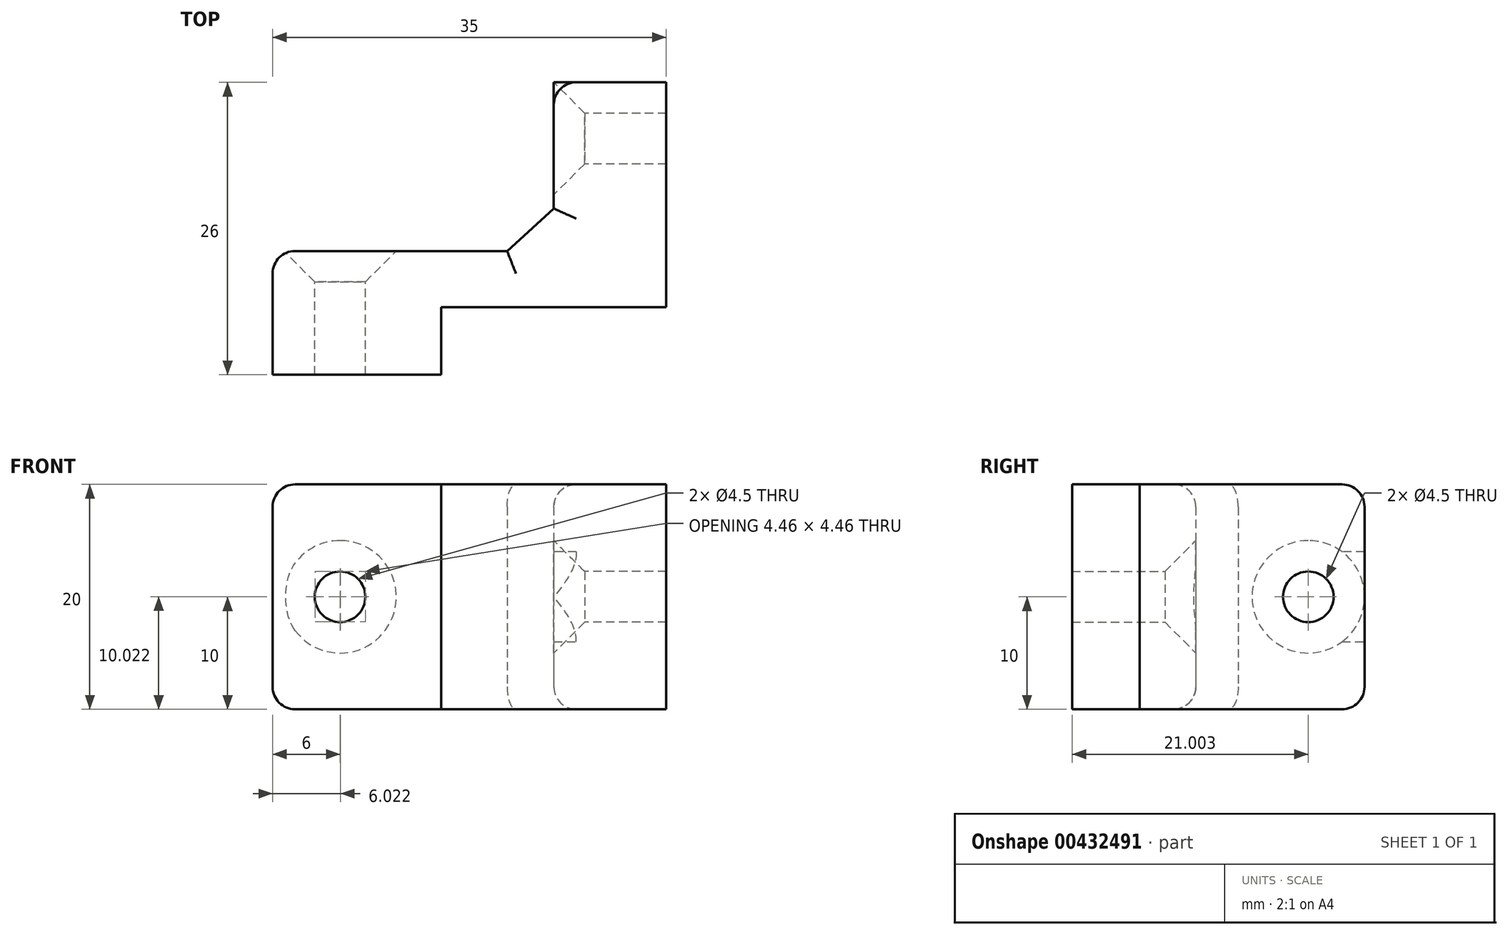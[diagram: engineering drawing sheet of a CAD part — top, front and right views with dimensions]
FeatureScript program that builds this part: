
annotation { "Feature Type Name" : "Feature", "Feature Type Description" : "" }
export const myFeature = defineFeature(function(context is Context, id is Id, definition is map)
    precondition{}
    {
        {
            var Q0;
            Q0=qCreatedBy(makeId("Top.planeOp"),FACE);
            var sketch = newSketch(context, id + "F0", { "sketchPlane" : qUnion([Q0])});
            skLineSegment(sketch, "E0", {"start": v(10, 0.5) * mm, "end": v(10, 20.5) * mm});
            skLineSegment(sketch, "E1", {"start": v(10, 20.5) * mm, "end": v(0, 20.5) * mm});
            skLineSegment(sketch, "E2", {"start": v(0, 20.5) * mm, "end": v(0, 9.28) * mm});
            skLineSegment(sketch, "E3", {"start": v(10, 0.5) * mm, "end": v(-10, 0.5) * mm});
            skLineSegment(sketch, "E4", {"start": v(-10, 0.5) * mm, "end": v(-10, -5.5) * mm});
            skLineSegment(sketch, "E5", {"start": v(-10, -5.5) * mm, "end": v(-25, -5.5) * mm});
            skLineSegment(sketch, "E6", {"start": v(-25, -5.5) * mm, "end": v(-25, 5.5) * mm});
            skLineSegment(sketch, "E7", {"start": v(-25, 5.5) * mm, "end": v(0, 5.5) * mm});
            skLineSegment(sketch, "E8", {"start": v(0, 9.28) * mm, "end": v(-4.14, 5.5) * mm});
            skSolve(sketch);
        }
        {
            var Q0;
            Q0=makeQuery(id+"F0.imprint","IMPRINT",FACE,{"disambiguationData":[TD([[makeQuery(id+"F0.imprint","IMPRINT",EDGE,{"derivedFrom":sQuery(id+"F0.wireOp",EDGE,"E0")}),1.0]])]});
            extrude(context, id + "F1", {"entities" : qUnion([Q0]), "depth" : 20 * mm});
        }
        {
            var Q0;
            Q0=makeQuery(id+"F1.opExtrude","SWEPT_FACE",FACE,{"disambiguationData":[OSD([sQuery(id+"F0.wireOp",EDGE,"E7")])]});
            var sketch = newSketch(context, id + "F2", { "sketchPlane" : qUnion([Q0])});
            skCircle(sketch, "E9", {"center": v(19, 10) * mm, "radius": 2 * mm});
            skSolve(sketch);
        }
        {
            var Q0;
            Q0=sQuery(id+"F2.wireOp",VERTEX,"E9.center");
            var Q1;
            Q1=makeQuery(id+"F1.opExtrude","SWEPT_BODY",BODY,{"disambiguationData":[OSD([sQuery(id+"F0.wireOp",EDGE,"E0"),sQuery(id+"F0.wireOp",EDGE,"E1"),sQuery(id+"F0.wireOp",EDGE,"E2"),sQuery(id+"F0.wireOp",EDGE,"E3"),sQuery(id+"F0.wireOp",EDGE,"E4"),sQuery(id+"F0.wireOp",EDGE,"E5"),sQuery(id+"F0.wireOp",EDGE,"E6"),sQuery(id+"F0.wireOp",EDGE,"E7"),sQuery(id+"F0.wireOp",EDGE,"E8")])]});
            hole(context, id + "F3", {"style" : HoleStyle.C_SINK, "endStyle" : HoleEndStyle.THROUGH, "holeDiameter" : 4.5 * mm, "cSinkDiameter" : 10 * mm, "cSinkAngle" : 90 * degree, "isTappedThrough" : true, "tappedDepth" : 12.7 * mm, "tapClearance" : 3, "locations" : qUnion([Q0]), "scope" : qUnion([Q1])});
        }
        {
            var Q0;
            Q0=makeQuery(id+"F1.opExtrude","SWEPT_FACE",FACE,{"disambiguationData":[OSD([sQuery(id+"F0.wireOp",EDGE,"E2")])]});
            var sketch = newSketch(context, id + "F4", { "sketchPlane" : qUnion([Q0])});
            skCircle(sketch, "E10", {"center": v(-15.5, 10) * mm, "radius": 2 * mm});
            skSolve(sketch);
        }
        {
            var Q0;
            Q0=sQuery(id+"F4.wireOp",VERTEX,"E10.center");
            var Q1;
            Q1=makeQuery(id+"F1.opExtrude","SWEPT_BODY",BODY,{"disambiguationData":[OSD([sQuery(id+"F0.wireOp",EDGE,"E0"),sQuery(id+"F0.wireOp",EDGE,"E1"),sQuery(id+"F0.wireOp",EDGE,"E2"),sQuery(id+"F0.wireOp",EDGE,"E3"),sQuery(id+"F0.wireOp",EDGE,"E4"),sQuery(id+"F0.wireOp",EDGE,"E5"),sQuery(id+"F0.wireOp",EDGE,"E6"),sQuery(id+"F0.wireOp",EDGE,"E7"),sQuery(id+"F0.wireOp",EDGE,"E8")])]});
            hole(context, id + "F5", {"style" : HoleStyle.C_SINK, "endStyle" : HoleEndStyle.THROUGH, "holeDiameter" : 4.5 * mm, "cSinkDiameter" : 10 * mm, "cSinkAngle" : 90 * degree, "isTappedThrough" : true, "tappedDepth" : 12.7 * mm, "tapClearance" : 3, "locations" : qUnion([Q0]), "scope" : qUnion([Q1])});
        }
        {
            var Q0;
            Q0=makeQuery(id+"F1.opExtrude","CAP_EDGE",EDGE,{"disambiguationData":[OSD([sQuery(id+"F0.wireOp",EDGE,"E2")])],"isStart":false});
            var Q1;
            Q1=makeQuery(id+"F1.opExtrude","CAP_EDGE",EDGE,{"disambiguationData":[OSD([sQuery(id+"F0.wireOp",EDGE,"E8")])],"isStart":false});
            var Q2;
            Q2=makeQuery(id+"F1.opExtrude","CAP_EDGE",EDGE,{"disambiguationData":[OSD([sQuery(id+"F0.wireOp",EDGE,"E7")])],"isStart":false});
            var Q3;
            Q3=makeQuery(id+"F1.opExtrude","SWEPT_EDGE",EDGE,{"disambiguationData":[OSD([sQuery(id+"F0.wireOp",EDGE,"E6"),sQuery(id+"F0.wireOp",EDGE,"E7")])]});
            var Q4;
            Q4=makeQuery(id+"F1.opExtrude","CAP_EDGE",EDGE,{"disambiguationData":[OSD([sQuery(id+"F0.wireOp",EDGE,"E7")])],"isStart":true});
            var Q5;
            Q5=makeQuery(id+"F1.opExtrude","CAP_EDGE",EDGE,{"disambiguationData":[OSD([sQuery(id+"F0.wireOp",EDGE,"E8")])],"isStart":true});
            var Q6;
            Q6=makeQuery(id+"F1.opExtrude","CAP_EDGE",EDGE,{"disambiguationData":[OSD([sQuery(id+"F0.wireOp",EDGE,"E2")])],"isStart":true});
            var Q7;
            {var subQ0=sQuery(id+"F0.wireOp",EDGE,"E2");var subQ1=sQuery(id+"F0.wireOp",EDGE,"E1");Q7=makeQuery(id+"F5.hole-0.boolean.opBoolean","SPLIT",EDGE,{"disambiguationData":[TD([makeQuery(id+"F1.opExtrude","CAP_FACE",FACE,{"disambiguationData":[OSD([sQuery(id+"F0.wireOp",EDGE,"E0"),subQ1,subQ0,sQuery(id+"F0.wireOp",EDGE,"E3"),sQuery(id+"F0.wireOp",EDGE,"E4"),sQuery(id+"F0.wireOp",EDGE,"E5"),sQuery(id+"F0.wireOp",EDGE,"E6"),sQuery(id+"F0.wireOp",EDGE,"E7"),sQuery(id+"F0.wireOp",EDGE,"E8")])],"isStart":false})])],"derivedFrom":makeQuery(id+"F1.opExtrude","SWEPT_EDGE",EDGE,{"disambiguationData":[OSD([subQ1,subQ0])]})});}
            var Q8;
            {var subQ0=sQuery(id+"F0.wireOp",EDGE,"E2");var subQ1=sQuery(id+"F0.wireOp",EDGE,"E1");Q8=makeQuery(id+"F5.hole-0.boolean.opBoolean","SPLIT",EDGE,{"disambiguationData":[TD([makeQuery(id+"F1.opExtrude","CAP_FACE",FACE,{"disambiguationData":[OSD([sQuery(id+"F0.wireOp",EDGE,"E0"),subQ1,subQ0,sQuery(id+"F0.wireOp",EDGE,"E3"),sQuery(id+"F0.wireOp",EDGE,"E4"),sQuery(id+"F0.wireOp",EDGE,"E5"),sQuery(id+"F0.wireOp",EDGE,"E6"),sQuery(id+"F0.wireOp",EDGE,"E7"),sQuery(id+"F0.wireOp",EDGE,"E8")])],"isStart":true})])],"derivedFrom":makeQuery(id+"F1.opExtrude","SWEPT_EDGE",EDGE,{"disambiguationData":[OSD([subQ1,subQ0])]})});}
            var Q9;
            Q9=makeQuery(id+"F1.opExtrude","CAP_EDGE",EDGE,{"disambiguationData":[OSD([sQuery(id+"F0.wireOp",EDGE,"E6")])],"isStart":false});
            var Q10;
            Q10=makeQuery(id+"F1.opExtrude","CAP_EDGE",EDGE,{"disambiguationData":[OSD([sQuery(id+"F0.wireOp",EDGE,"E6")])],"isStart":true});
            var Q11;
            Q11=makeQuery(id+"F1.opExtrude","CAP_EDGE",EDGE,{"disambiguationData":[OSD([sQuery(id+"F0.wireOp",EDGE,"E1")])],"isStart":false});
            var Q12;
            Q12=makeQuery(id+"F1.opExtrude","CAP_EDGE",EDGE,{"disambiguationData":[OSD([sQuery(id+"F0.wireOp",EDGE,"E1")])],"isStart":true});
            fillet(context, id + "F6", {"entities" : qUnion([Q0, Q1, Q2, Q3, Q4, Q5, Q6, Q7, Q8, Q9, Q10, Q11, Q12]), "radius" : 2 * mm, "tangentPropagation" : true, "allowEdgeOverflow" : false});
        }
    });
